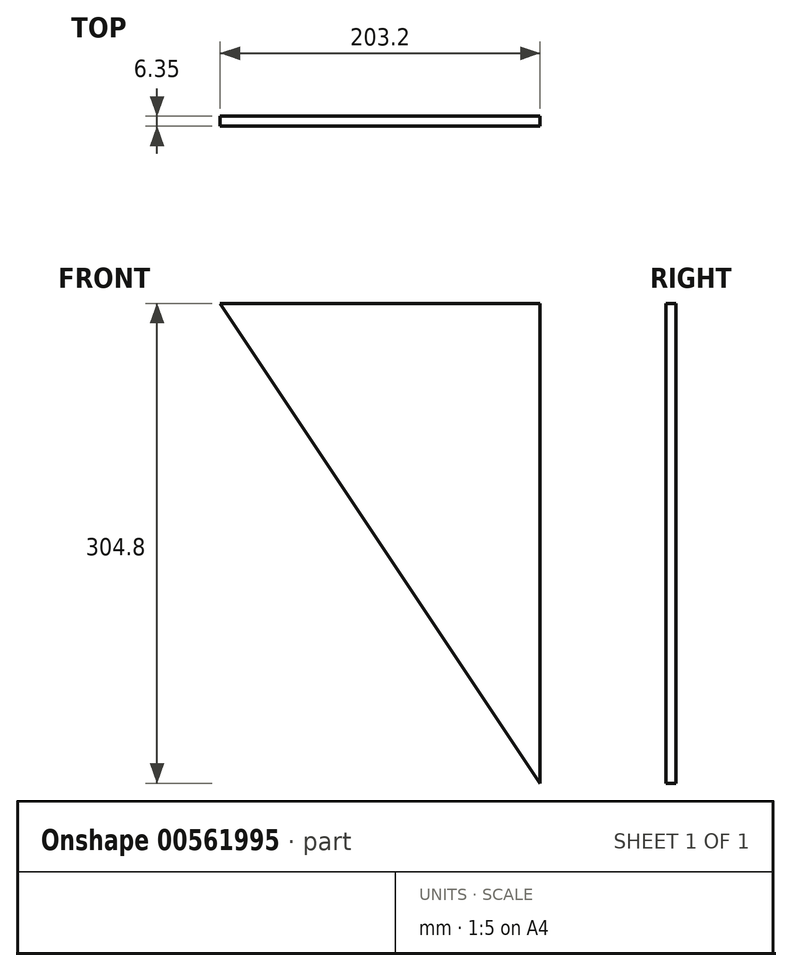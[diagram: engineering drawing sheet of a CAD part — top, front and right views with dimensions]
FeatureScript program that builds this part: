
annotation { "Feature Type Name" : "Feature", "Feature Type Description" : "" }
export const myFeature = defineFeature(function(context is Context, id is Id, definition is map)
    precondition{}
    {
        {
            var Q0;
            Q0=qCreatedBy(makeId("Front.planeOp"),FACE);
            var sketch = newSketch(context, id + "F0", { "sketchPlane" : qUnion([Q0])});
            skLineSegment(sketch, "E0", {"start": v(0, 0) * mm, "end": v(203.2, 0) * mm});
            skLineSegment(sketch, "E1", {"start": v(203.2, 0) * mm, "end": v(203.2, -304.8) * mm});
            skLineSegment(sketch, "E2", {"start": v(203.2, -304.8) * mm, "end": v(0, 0) * mm});
            skSolve(sketch);
        }
        {
            var Q0;
            Q0 = qSketchRegion(id + "F0", true);
            extrude(context, id + "F1", {"entities" : qUnion([Q0]), "depth" : 6.35 * mm, "offsetDistance" : 25.4 * mm});
        }
    });
